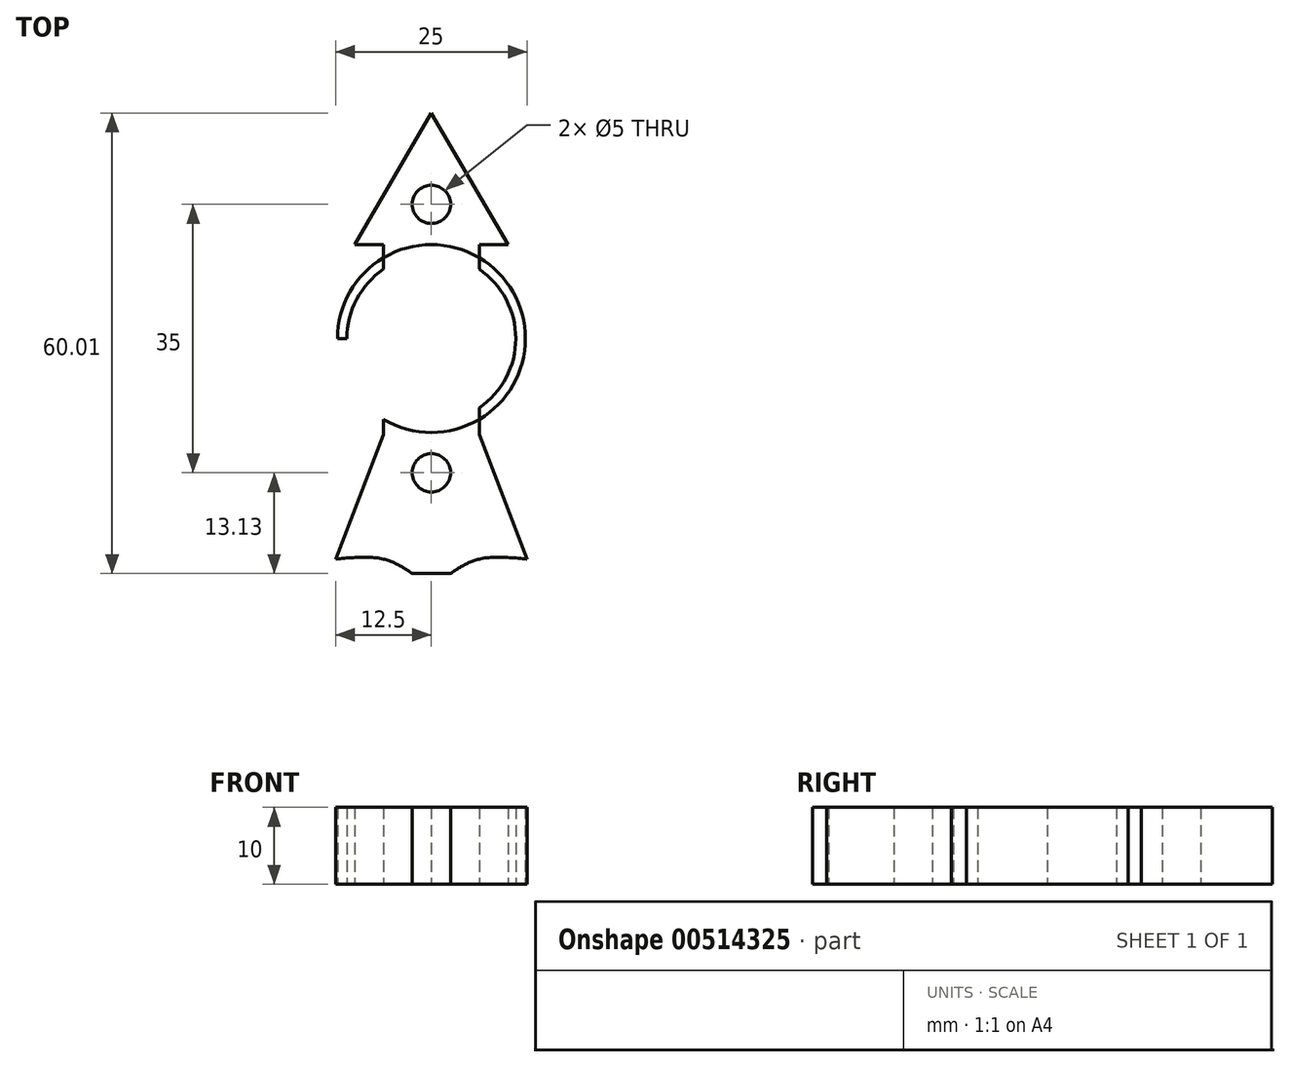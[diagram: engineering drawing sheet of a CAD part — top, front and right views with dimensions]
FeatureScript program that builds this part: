
annotation { "Feature Type Name" : "Feature", "Feature Type Description" : "" }
export const myFeature = defineFeature(function(context is Context, id is Id, definition is map)
    precondition{}
    {
        {
            var Q0;
            Q0=qCreatedBy(makeId("Top.planeOp"),FACE);
            var sketch = newSketch(context, id + "F0", { "sketchPlane" : qUnion([Q0])});
            skLineSegment(sketch, "E0", {"start": v(0, -32.5) * mm, "end": v(-12.5, -32.5) * mm});
            skLineSegment(sketch, "E1", {"start": v(-12.5, -32.5) * mm, "end": v(12.5, -32.5) * mm});
            skCircle(sketch, "E2", {"center": v(0, -32.5) * mm, "radius": 11 * mm});
            skCircle(sketch, "E3", {"center": v(0, -32.5) * mm, "radius": 12.25 * mm});
            skCircle(sketch, "E4", {"center": v(0, -15) * mm, "radius": 2.5 * mm});
            skLineSegment(sketch, "E5", {"start": v(-6.25, -45) * mm, "end": v(6.25, -45) * mm});
            skLineSegment(sketch, "E6", {"start": v(6.25, -45) * mm, "end": v(6.25, -43.04) * mm});
            skLineSegment(sketch, "E7", {"start": v(-6.25, -45) * mm, "end": v(-6.25, -43.04) * mm});
            skLineSegment(sketch, "E8", {"start": v(6.25, -45) * mm, "end": v(6.25, -18.44) * mm});
            skLineSegment(sketch, "E9", {"start": v(-6.25, -45) * mm, "end": v(-6.25, -61.25) * mm});
            skLineSegment(sketch, "E10", {"start": v(6.25, -45) * mm, "end": v(6.25, -61.25) * mm});
            skLineSegment(sketch, "E11", {"start": v(-6.25, -45) * mm, "end": v(-12.5, -61.25) * mm});
            skLineSegment(sketch, "E12", {"start": v(6.25, -45) * mm, "end": v(12.5, -61.25) * mm});
            skLineSegment(sketch, "E13", {"start": v(0, -47.5) * mm, "end": v(0, -50) * mm});
            skCircle(sketch, "E14", {"center": v(0, -50) * mm, "radius": 2.5 * mm});
            skLineSegment(sketch, "E15", {"start": v(-6.25, -61.25) * mm, "end": v(6.25, -61.25) * mm});
            skLineSegment(sketch, "E16", {"start": v(0, -63.12) * mm, "end": v(0, -61.25) * mm});
            skLineSegment(sketch, "E17", {"start": v(0, -63.12) * mm, "end": v(-2.5, -63.12) * mm});
            skLineSegment(sketch, "E18", {"start": v(0, -63.12) * mm, "end": v(2.5, -63.12) * mm});
            skFitSpline(sketch, "E19", {"points": [v(-12.5, -61.25) * mm, v(-6.25, -61.25) * mm, v(-2.5, -63.12) * mm], "startDerivative": vector(12.2, 1.14) * mm, "endDerivative": vector(7.64, -5.1) * mm});
            skFitSpline(sketch, "E20", {"points": [v(2.5, -63.12) * mm, v(6.25, -61.25) * mm, v(12.5, -61.25) * mm], "startDerivative": vector(7.64, 5.1) * mm, "endDerivative": vector(12.2, -1.14) * mm});
            skLineSegment(sketch, "E21", {"start": v(0, -20.25) * mm, "end": v(-10, -20.25) * mm});
            skLineSegment(sketch, "E22", {"start": v(0, -20.25) * mm, "end": v(10, -20.25) * mm});
            skLineSegment(sketch, "E23", {"start": v(0, -20.25) * mm, "end": v(0, -3.13) * mm});
            skLineSegment(sketch, "E24", {"start": v(0, -3.13) * mm, "end": v(-10, -20.25) * mm});
            skLineSegment(sketch, "E25", {"start": v(0, -3.13) * mm, "end": v(10, -20.25) * mm});
            skLineSegment(sketch, "E26", {"start": v(-6.25, -43.04) * mm, "end": v(-6.25, -20.25) * mm});
            skPoint(sketch, "E26.endSnap0", {"position": v(-6.25, -32.5) * mm});
            skSolve(sketch);
        }
        {
            var Q0;
            {var subQ1=sQuery(id+"F0.wireOp",EDGE,"E21");Q0=makeQuery(id+"F0.imprint","IMPRINT",FACE,{"disambiguationData":[TD([[makeQuery(id+"F0.imprint","IMPRINT",EDGE,{"derivedFrom":subQ1}),-1.0]])]});}
            var Q1;
            {var subQ6=sQuery(id+"F0.wireOp",EDGE,"E25");Q1=makeQuery(id+"F0.imprint","IMPRINT",FACE,{"disambiguationData":[TD([[makeQuery(id+"F0.imprint","IMPRINT",EDGE,{"derivedFrom":subQ6}),-1.0]])]});}
            var Q2;
            {var subQ0=sQuery(id+"F0.wireOp",EDGE,"E3");var subQ4=sQuery(id+"F0.wireOp",EDGE,"E1");var subQ5=makeQuery(id+"F0.imprint","INTERSECT",VERTEX,{"disambiguationData":[OD(0.0)],"derivedFrom":[subQ4,subQ0]});Q2=makeQuery(id+"F0.imprint","IMPRINT",FACE,{"disambiguationData":[TD([[makeQuery(id+"F0.imprint","IMPRINT",EDGE,{"disambiguationData":[TD([[subQ5,-1.0]])],"derivedFrom":subQ4}),-1.0]])]});}
            var Q3;
            {var subQ0=sQuery(id+"F0.wireOp",EDGE,"E3");var subQ1=sQuery(id+"F0.wireOp",EDGE,"E1");var subQ2=makeQuery(id+"F0.imprint","INTERSECT",VERTEX,{"disambiguationData":[OD(1.0)],"derivedFrom":[subQ1,subQ0]});Q3=makeQuery(id+"F0.imprint","IMPRINT",FACE,{"disambiguationData":[TD([[makeQuery(id+"F0.imprint","IMPRINT",EDGE,{"disambiguationData":[TD([[subQ2,1.0]])],"derivedFrom":subQ1}),-1.0]])]});}
            var Q4;
            {var subQ0=sQuery(id+"F0.wireOp",EDGE,"E3");var subQ1=sQuery(id+"F0.wireOp",EDGE,"E1");var subQ2=makeQuery(id+"F0.imprint","INTERSECT",VERTEX,{"disambiguationData":[OD(1.0)],"derivedFrom":[subQ1,subQ0]});Q4=makeQuery(id+"F0.imprint","IMPRINT",FACE,{"disambiguationData":[TD([[makeQuery(id+"F0.imprint","IMPRINT",EDGE,{"disambiguationData":[TD([[subQ2,1.0]])],"derivedFrom":subQ1}),1.0]])]});}
            var Q5;
            {var subQ0=sQuery(id+"F0.wireOp",EDGE,"E3");var subQ2=sQuery(id+"F0.wireOp",EDGE,"E1");var subQ3=makeQuery(id+"F0.imprint","INTERSECT",VERTEX,{"disambiguationData":[OD(0.0)],"derivedFrom":[subQ2,subQ0]});Q5=makeQuery(id+"F0.imprint","IMPRINT",FACE,{"disambiguationData":[TD([[makeQuery(id+"F0.imprint","IMPRINT",EDGE,{"disambiguationData":[TD([[subQ3,-1.0]])],"derivedFrom":subQ2}),1.0]])]});}
            var Q6;
            {var subQ0=sQuery(id+"F0.wireOp",EDGE,"E10");Q6=makeQuery(id+"F0.imprint","IMPRINT",FACE,{"disambiguationData":[TD([[makeQuery(id+"F0.imprint","IMPRINT",EDGE,{"derivedFrom":subQ0}),1.0]])]});}
            var Q7;
            Q7=makeQuery(id+"F0.imprint","IMPRINT",FACE,{"disambiguationData":[TD([[makeQuery(id+"F0.imprint","IMPRINT",EDGE,{"derivedFrom":sQuery(id+"F0.wireOp",EDGE,"E5")}),-1.0]])]});
            var Q8;
            {var subQ0=sQuery(id+"F0.wireOp",EDGE,"E9");Q8=makeQuery(id+"F0.imprint","IMPRINT",FACE,{"disambiguationData":[TD([[makeQuery(id+"F0.imprint","IMPRINT",EDGE,{"derivedFrom":subQ0}),-1.0]])]});}
            var Q9;
            {var subQ3=sQuery(id+"F0.wireOp",EDGE,"E16");Q9=makeQuery(id+"F0.imprint","IMPRINT",FACE,{"disambiguationData":[TD([[makeQuery(id+"F0.imprint","IMPRINT",EDGE,{"derivedFrom":subQ3}),-1.0]])]});}
            var Q10;
            {var subQ3=sQuery(id+"F0.wireOp",EDGE,"E16");Q10=makeQuery(id+"F0.imprint","IMPRINT",FACE,{"disambiguationData":[TD([[makeQuery(id+"F0.imprint","IMPRINT",EDGE,{"derivedFrom":subQ3}),1.0]])]});}
            var Q11;
            {var subQ4=sQuery(id+"F0.wireOp",EDGE,"E8");var subQ6=sQuery(id+"F0.wireOp",EDGE,"E2");var subQ7=makeQuery(id+"F0.imprint","INTERSECT",VERTEX,{"disambiguationData":[OD(0.0)],"derivedFrom":[subQ6,subQ4]});Q11=makeQuery(id+"F0.imprint","IMPRINT",FACE,{"disambiguationData":[TD([[makeQuery(id+"F0.imprint","IMPRINT",EDGE,{"disambiguationData":[TD([[subQ7,-1.0]])],"derivedFrom":subQ6}),-1.0]])]});}
            var Q12;
            {var subQ0=sQuery(id+"F0.wireOp",EDGE,"E26");var subQ1=sQuery(id+"F0.wireOp",EDGE,"E2");var subQ2=makeQuery(id+"F0.imprint","INTERSECT",VERTEX,{"disambiguationData":[OD(1.0)],"derivedFrom":[subQ1,subQ0]});Q12=makeQuery(id+"F0.imprint","IMPRINT",FACE,{"disambiguationData":[TD([[makeQuery(id+"F0.imprint","IMPRINT",EDGE,{"disambiguationData":[TD([[subQ2,-1.0]])],"derivedFrom":subQ1}),-1.0]])]});}
            var Q13;
            {var subQ4=sQuery(id+"F0.wireOp",EDGE,"E5");Q13=makeQuery(id+"F0.imprint","IMPRINT",FACE,{"disambiguationData":[TD([[makeQuery(id+"F0.imprint","IMPRINT",EDGE,{"derivedFrom":subQ4}),1.0]])]});}
            var Q14;
            {var subQ0=sQuery(id+"F0.wireOp",EDGE,"E21");var subQ3=sQuery(id+"F0.wireOp",EDGE,"E26");var subQ5=makeQuery(id+"F0.imprint","INTERSECT",VERTEX,{"derivedFrom":[subQ0,subQ3]});Q14=makeQuery(id+"F0.imprint","IMPRINT",FACE,{"disambiguationData":[TD([[makeQuery(id+"F0.imprint","IMPRINT",EDGE,{"disambiguationData":[TD([[subQ5,1.0]])],"derivedFrom":subQ3}),-1.0]])]});}
            var Q15;
            {var subQ0=sQuery(id+"F0.wireOp",EDGE,"E22");var subQ3=sQuery(id+"F0.wireOp",EDGE,"E8");var subQ5=makeQuery(id+"F0.imprint","INTERSECT",VERTEX,{"derivedFrom":[subQ3,subQ0]});Q15=makeQuery(id+"F0.imprint","IMPRINT",FACE,{"disambiguationData":[TD([[makeQuery(id+"F0.imprint","IMPRINT",EDGE,{"disambiguationData":[TD([[subQ5,1.0]])],"derivedFrom":subQ3}),1.0]])]});}
            extrude(context, id + "F1", {"entities" : qUnion([Q0, Q1, Q2, Q3, Q4, Q5, Q6, Q7, Q8, Q9, Q10, Q11, Q12, Q13, Q14, Q15]), "depth" : 10 * mm, "offsetDistance" : 25 * mm});
        }
    });
